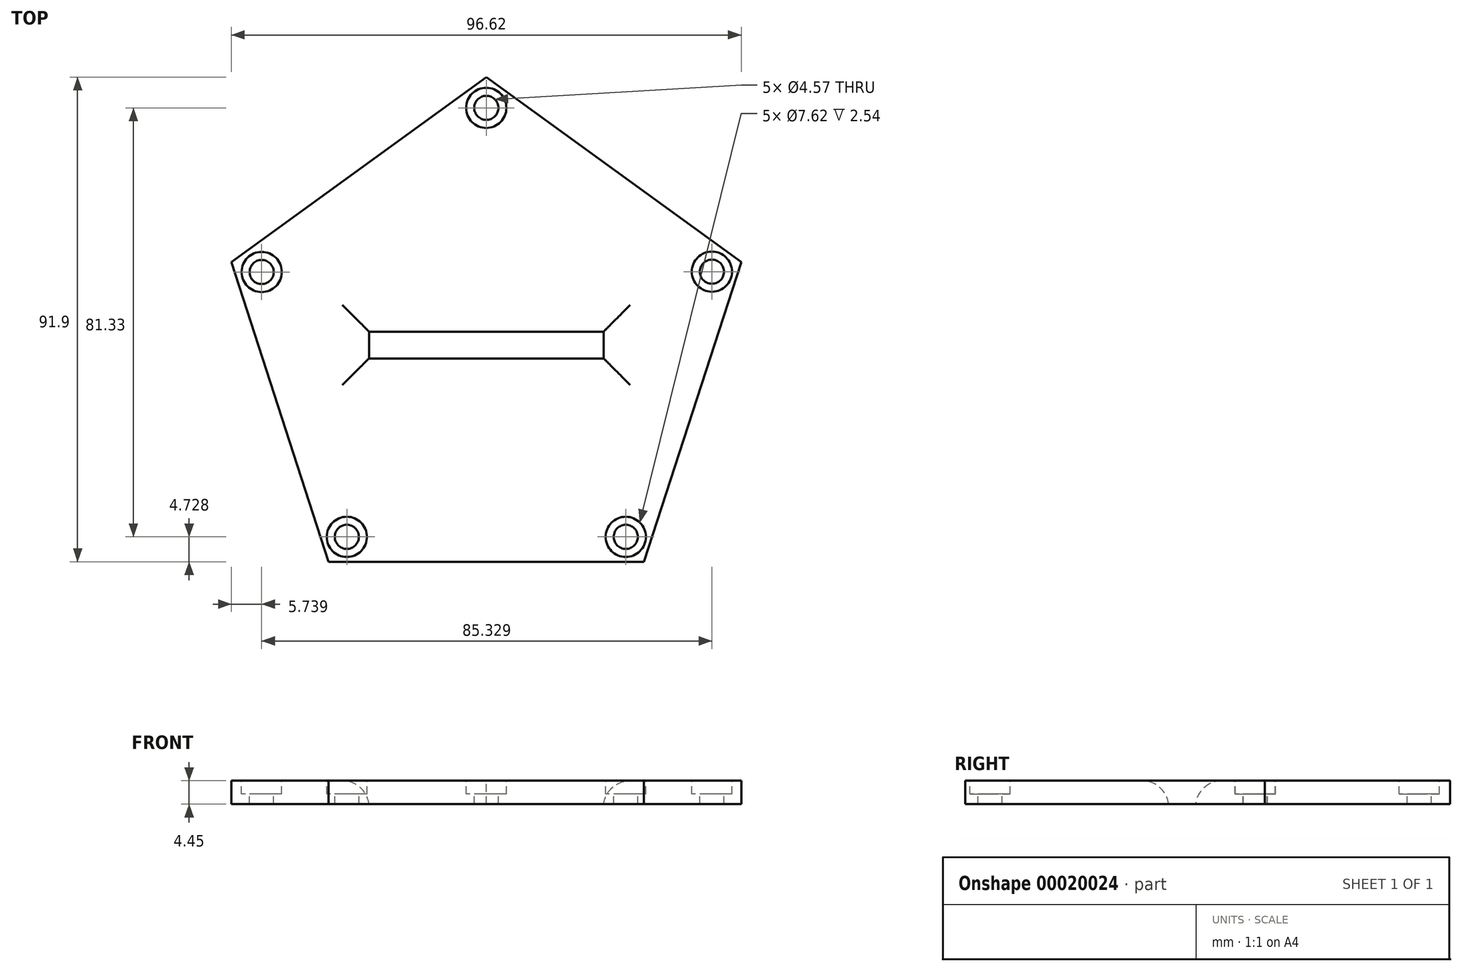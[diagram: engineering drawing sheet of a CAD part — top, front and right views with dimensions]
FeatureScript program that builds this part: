
annotation { "Feature Type Name" : "Feature", "Feature Type Description" : "" }
export const myFeature = defineFeature(function(context is Context, id is Id, definition is map)
    precondition{}
    {
        {
            var Q0;
            Q0=qCreatedBy(makeId("Top.planeOp"),FACE);
            var sketch = newSketch(context, id + "F0", { "sketchPlane" : qUnion([Q0])});
            skCircle(sketch, "E0", {"center": v(0, 0) * mm, "radius": 50.8 * mm});
            skCircle(sketch, "E1.cCircle", {"center": v(0, 0) * mm, "radius": 50.8 * mm, "construction": true});
            skLineSegment(sketch, "E1.0", {"start": v(-29.86, -41.1) * mm, "end": v(-48.31, 15.7) * mm});
            skLineSegment(sketch, "E1.1", {"start": v(-48.31, 15.7) * mm, "end": v(0, 50.8) * mm});
            skLineSegment(sketch, "E1.2", {"start": v(0, 50.8) * mm, "end": v(48.31, 15.7) * mm});
            skLineSegment(sketch, "E1.3", {"start": v(48.31, 15.7) * mm, "end": v(29.86, -41.1) * mm});
            skLineSegment(sketch, "E1.4", {"start": v(29.86, -41.1) * mm, "end": v(-29.86, -41.1) * mm});
            skCircle(sketch, "E2", {"center": v(0, 0) * mm, "radius": 48.77 * mm});
            skLineSegment(sketch, "E3", {"start": v(-48.31, 15.7) * mm, "end": v(39.09, -12.7) * mm, "construction": true});
            skLineSegment(sketch, "E4", {"start": v(-29.86, -41.1) * mm, "end": v(24.16, 33.25) * mm, "construction": true});
            skLineSegment(sketch, "E5", {"start": v(0, 50.8) * mm, "end": v(0, -41.1) * mm, "construction": true});
            skLineSegment(sketch, "E6", {"start": v(29.86, -41.1) * mm, "end": v(-24.16, 33.25) * mm, "construction": true});
            skPoint(sketch, "E7", {"position": v(0, 48.77) * mm});
            skLineSegment(sketch, "E8", {"start": v(48.31, 15.7) * mm, "end": v(-39.09, -12.7) * mm, "construction": true});
            skPoint(sketch, "E9", {"position": v(46.38, 15.07) * mm});
            skPoint(sketch, "E10", {"position": v(-46.38, 15.07) * mm});
            skPoint(sketch, "E11", {"position": v(-28.67, -39.45) * mm});
            skPoint(sketch, "E12", {"position": v(28.67, -39.45) * mm});
            skPoint(sketch, "E13", {"position": v(-42.57, 13.83) * mm});
            skPoint(sketch, "E14", {"position": v(0, 44.96) * mm});
            skPoint(sketch, "E15", {"position": v(42.76, 13.9) * mm});
            skPoint(sketch, "E16", {"position": v(26.43, -36.37) * mm});
            skPoint(sketch, "E17", {"position": v(-26.43, -36.37) * mm});
            skCircle(sketch, "E18", {"center": v(-42.57, 13.83) * mm, "radius": 3.81 * mm});
            skCircle(sketch, "E19", {"center": v(-26.43, -36.37) * mm, "radius": 3.81 * mm});
            skCircle(sketch, "E20", {"center": v(0, 44.96) * mm, "radius": 3.81 * mm});
            skCircle(sketch, "E21", {"center": v(26.43, -36.37) * mm, "radius": 3.81 * mm});
            skCircle(sketch, "E22", {"center": v(42.76, 13.9) * mm, "radius": 3.81 * mm});
            skCircle(sketch, "E23", {"center": v(-42.57, 13.83) * mm, "radius": 2.29 * mm});
            skCircle(sketch, "E24", {"center": v(-26.43, -36.37) * mm, "radius": 2.29 * mm});
            skCircle(sketch, "E25", {"center": v(26.43, -36.37) * mm, "radius": 2.29 * mm});
            skCircle(sketch, "E26", {"center": v(42.76, 13.9) * mm, "radius": 2.29 * mm});
            skCircle(sketch, "E27", {"center": v(0, 44.96) * mm, "radius": 2.29 * mm});
            skLineSegment(sketch, "E28", {"start": v(-48.31, 15.7) * mm, "end": v(48.31, 15.7) * mm, "construction": true});
            skLineSegment(sketch, "E29.rect.bottom", {"start": v(22.23, 2.54) * mm, "end": v(-22.22, 2.54) * mm});
            skLineSegment(sketch, "E29.rect.top", {"start": v(22.23, -2.54) * mm, "end": v(-22.22, -2.54) * mm});
            skLineSegment(sketch, "E29.rect.left", {"start": v(22.23, 2.54) * mm, "end": v(22.23, -2.54) * mm});
            skLineSegment(sketch, "E29.rect.right", {"start": v(-22.22, 2.54) * mm, "end": v(-22.22, -2.54) * mm});
            skSolve(sketch);
        }
        {
            var Q0;
            Q0=makeQuery(id+"F0.imprint","IMPRINT",FACE,{"disambiguationData":[TD([[makeQuery(id+"F0.imprint","IMPRINT",EDGE,{"derivedFrom":sQuery(id+"F0.wireOp",EDGE,"E18")}),-1.0]])]});
            var Q1;
            {var subQ0=sQuery(id+"F0.wireOp",EDGE,"E2");var subQ3=makeQuery(id+"F0.imprint","INTERSECT",VERTEX,{"derivedFrom":[subQ0,sQuery(id+"F0.wireOp",EDGE,"E19")]});Q1=makeQuery(id+"F0.imprint","IMPRINT",FACE,{"disambiguationData":[TD([[makeQuery(id+"F0.imprint","IMPRINT",EDGE,{"disambiguationData":[TD([[subQ3,1.0]])],"derivedFrom":subQ0}),-1.0]])]});}
            var Q2;
            {var subQ0=sQuery(id+"F0.wireOp",EDGE,"E2");var subQ3=sQuery(id+"F0.wireOp",EDGE,"E1.0");var subQ4=makeQuery(id+"F0.imprint","INTERSECT",VERTEX,{"disambiguationData":[OD(1.0)],"derivedFrom":[subQ3,subQ0]});Q2=makeQuery(id+"F0.imprint","IMPRINT",FACE,{"disambiguationData":[TD([[makeQuery(id+"F0.imprint","IMPRINT",EDGE,{"disambiguationData":[TD([[subQ4,1.0]])],"derivedFrom":subQ0}),-1.0]])]});}
            var Q3;
            {var subQ0=sQuery(id+"F0.wireOp",EDGE,"E2");var subQ3=makeQuery(id+"F0.imprint","INTERSECT",VERTEX,{"derivedFrom":[subQ0,sQuery(id+"F0.wireOp",EDGE,"E20")]});Q3=makeQuery(id+"F0.imprint","IMPRINT",FACE,{"disambiguationData":[TD([[makeQuery(id+"F0.imprint","IMPRINT",EDGE,{"disambiguationData":[TD([[subQ3,1.0]])],"derivedFrom":subQ0}),-1.0]])]});}
            var Q4;
            {var subQ0=sQuery(id+"F0.wireOp",EDGE,"E2");var subQ3=makeQuery(id+"F0.imprint","INTERSECT",VERTEX,{"derivedFrom":[subQ0,sQuery(id+"F0.wireOp",EDGE,"E22")]});Q4=makeQuery(id+"F0.imprint","IMPRINT",FACE,{"disambiguationData":[TD([[makeQuery(id+"F0.imprint","IMPRINT",EDGE,{"disambiguationData":[TD([[subQ3,1.0]])],"derivedFrom":subQ0}),-1.0]])]});}
            var Q5;
            {var subQ0=sQuery(id+"F0.wireOp",EDGE,"E2");var subQ3=makeQuery(id+"F0.imprint","INTERSECT",VERTEX,{"derivedFrom":[subQ0,sQuery(id+"F0.wireOp",EDGE,"E21")]});Q5=makeQuery(id+"F0.imprint","IMPRINT",FACE,{"disambiguationData":[TD([[makeQuery(id+"F0.imprint","IMPRINT",EDGE,{"disambiguationData":[TD([[subQ3,1.0]])],"derivedFrom":subQ0}),-1.0]])]});}
            var Q6;
            Q6=makeQuery(id+"F0.imprint","IMPRINT",FACE,{"disambiguationData":[TD([[makeQuery(id+"F0.imprint","IMPRINT",EDGE,{"derivedFrom":sQuery(id+"F0.wireOp",EDGE,"E22")}),1.0]])]});
            var Q7;
            Q7=makeQuery(id+"F0.imprint","IMPRINT",FACE,{"disambiguationData":[TD([[makeQuery(id+"F0.imprint","IMPRINT",EDGE,{"derivedFrom":sQuery(id+"F0.wireOp",EDGE,"E21")}),1.0]])]});
            var Q8;
            Q8=makeQuery(id+"F0.imprint","IMPRINT",FACE,{"disambiguationData":[TD([[makeQuery(id+"F0.imprint","IMPRINT",EDGE,{"derivedFrom":sQuery(id+"F0.wireOp",EDGE,"E20")}),1.0]])]});
            var Q9;
            Q9=makeQuery(id+"F0.imprint","IMPRINT",FACE,{"disambiguationData":[TD([[makeQuery(id+"F0.imprint","IMPRINT",EDGE,{"derivedFrom":sQuery(id+"F0.wireOp",EDGE,"E18")}),1.0]])]});
            var Q10;
            Q10=makeQuery(id+"F0.imprint","IMPRINT",FACE,{"disambiguationData":[TD([[makeQuery(id+"F0.imprint","IMPRINT",EDGE,{"derivedFrom":sQuery(id+"F0.wireOp",EDGE,"E19")}),1.0]])]});
            extrude(context, id + "F1", {"entities" : qUnion([Q0, Q1, Q2, Q3, Q4, Q5, Q6, Q7, Q8, Q9, Q10]), "oppositeDirection" : true, "depth" : 4.44 * mm});
        }
        {
            var Q0;
            Q0=makeQuery(id+"F0.imprint","IMPRINT",FACE,{"disambiguationData":[TD([[makeQuery(id+"F0.imprint","IMPRINT",EDGE,{"derivedFrom":sQuery(id+"F0.wireOp",EDGE,"E21")}),1.0]])]});
            var Q1;
            Q1=makeQuery(id+"F0.imprint","IMPRINT",FACE,{"disambiguationData":[TD([[makeQuery(id+"F0.imprint","IMPRINT",EDGE,{"derivedFrom":sQuery(id+"F0.wireOp",EDGE,"E22")}),1.0]])]});
            var Q2;
            Q2=makeQuery(id+"F0.imprint","IMPRINT",FACE,{"disambiguationData":[TD([[makeQuery(id+"F0.imprint","IMPRINT",EDGE,{"derivedFrom":sQuery(id+"F0.wireOp",EDGE,"E19")}),1.0]])]});
            var Q3;
            Q3=makeQuery(id+"F0.imprint","IMPRINT",FACE,{"disambiguationData":[TD([[makeQuery(id+"F0.imprint","IMPRINT",EDGE,{"derivedFrom":sQuery(id+"F0.wireOp",EDGE,"E18")}),1.0]])]});
            var Q4;
            Q4=makeQuery(id+"F0.imprint","IMPRINT",FACE,{"disambiguationData":[TD([[makeQuery(id+"F0.imprint","IMPRINT",EDGE,{"derivedFrom":sQuery(id+"F0.wireOp",EDGE,"E20")}),1.0]])]});
            extrude(context, id + "F2", {"entities" : qUnion([Q0, Q1, Q2, Q3, Q4]), "operationType" : NewBodyOperationType.REMOVE, "oppositeDirection" : true, "depth" : 2.54 * mm});
        }
        {
            var Q0;
            Q0=makeQuery(id+"F1.opExtrude","CAP_EDGE",EDGE,{"disambiguationData":[OSD([sQuery(id+"F0.wireOp",EDGE,"E29.rect.bottom")])],"isStart":true});
            var Q1;
            Q1=makeQuery(id+"F1.opExtrude","CAP_EDGE",EDGE,{"disambiguationData":[OSD([sQuery(id+"F0.wireOp",EDGE,"E29.rect.right")])],"isStart":true});
            var Q2;
            Q2=makeQuery(id+"F1.opExtrude","CAP_EDGE",EDGE,{"disambiguationData":[OSD([sQuery(id+"F0.wireOp",EDGE,"E29.rect.top")])],"isStart":true});
            var Q3;
            Q3=makeQuery(id+"F1.opExtrude","CAP_EDGE",EDGE,{"disambiguationData":[OSD([sQuery(id+"F0.wireOp",EDGE,"E29.rect.left")])],"isStart":true});
            fillet(context, id + "F3", {"entities" : qUnion([Q0, Q1, Q2, Q3]), "radius" : 5.08 * mm, "tangentPropagation" : true, "allowEdgeOverflow" : false});
        }
    });
